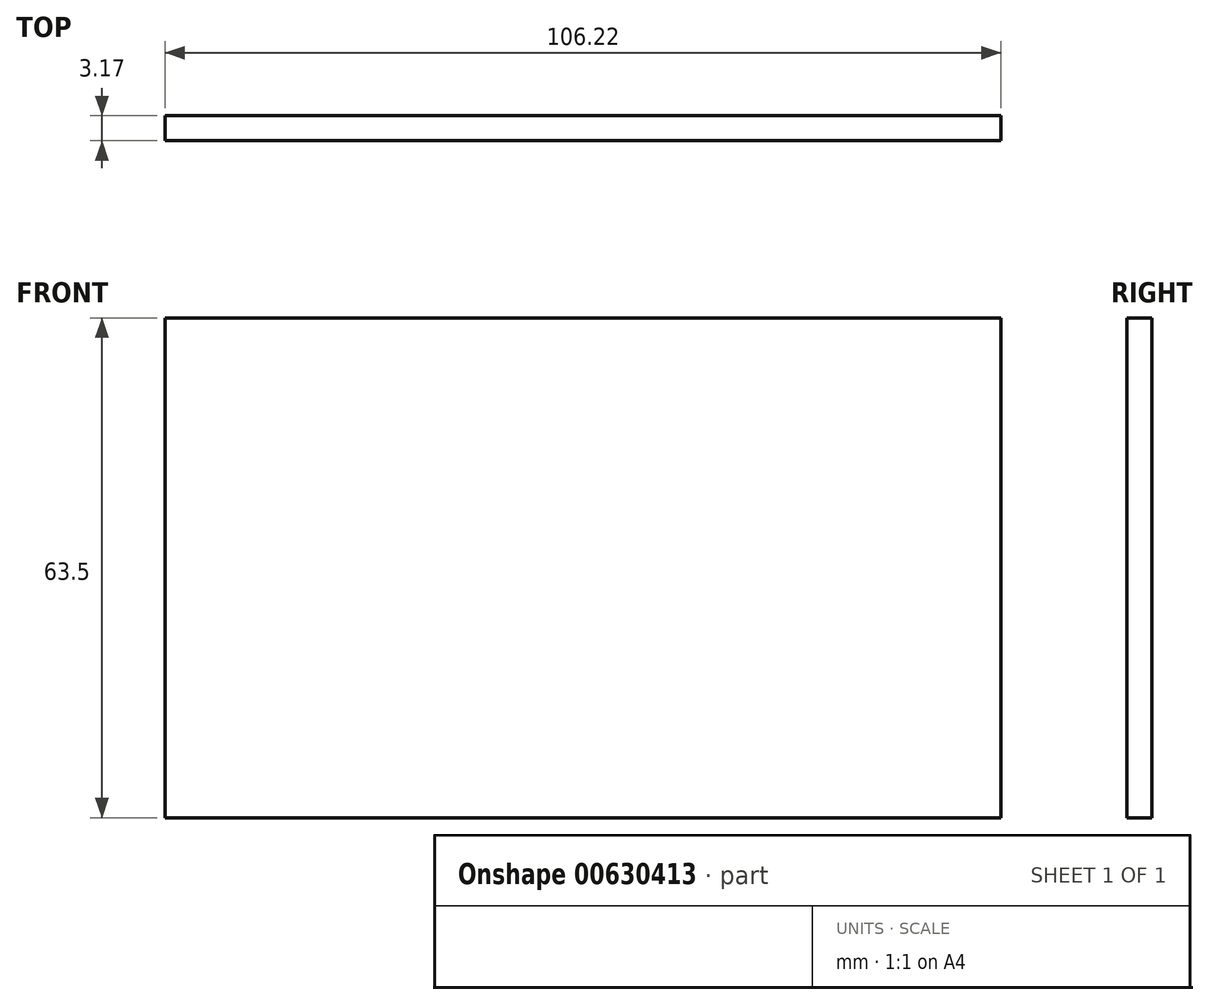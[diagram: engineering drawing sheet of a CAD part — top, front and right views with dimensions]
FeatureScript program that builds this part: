
annotation { "Feature Type Name" : "Feature", "Feature Type Description" : "" }
export const myFeature = defineFeature(function(context is Context, id is Id, definition is map)
    precondition{}
    {
        {
            var Q0;
            Q0=qCreatedBy(makeId("Front.planeOp"),FACE);
            var sketch = newSketch(context, id + "F0", { "sketchPlane" : qUnion([Q0])});
            skLineSegment(sketch, "E0.bottom", {"start": v(53.11, 31.75) * mm, "end": v(-53.11, 31.75) * mm});
            skLineSegment(sketch, "E0.top", {"start": v(53.11, -31.75) * mm, "end": v(-53.11, -31.75) * mm});
            skLineSegment(sketch, "E0.left", {"start": v(53.11, 31.75) * mm, "end": v(53.11, -31.75) * mm});
            skLineSegment(sketch, "E0.right", {"start": v(-53.11, 31.75) * mm, "end": v(-53.11, -31.75) * mm});
            skPoint(sketch, "E0.middle", {"position": v(0, 0) * mm});
            skSolve(sketch);
        }
        {
            var Q0;
            Q0 = qSketchRegion(id + "F0", true);
            extrude(context, id + "F1", {"entities" : qUnion([Q0]), "depth" : 3.17 * mm, "offsetDistance" : 25.4 * mm});
        }
    });
